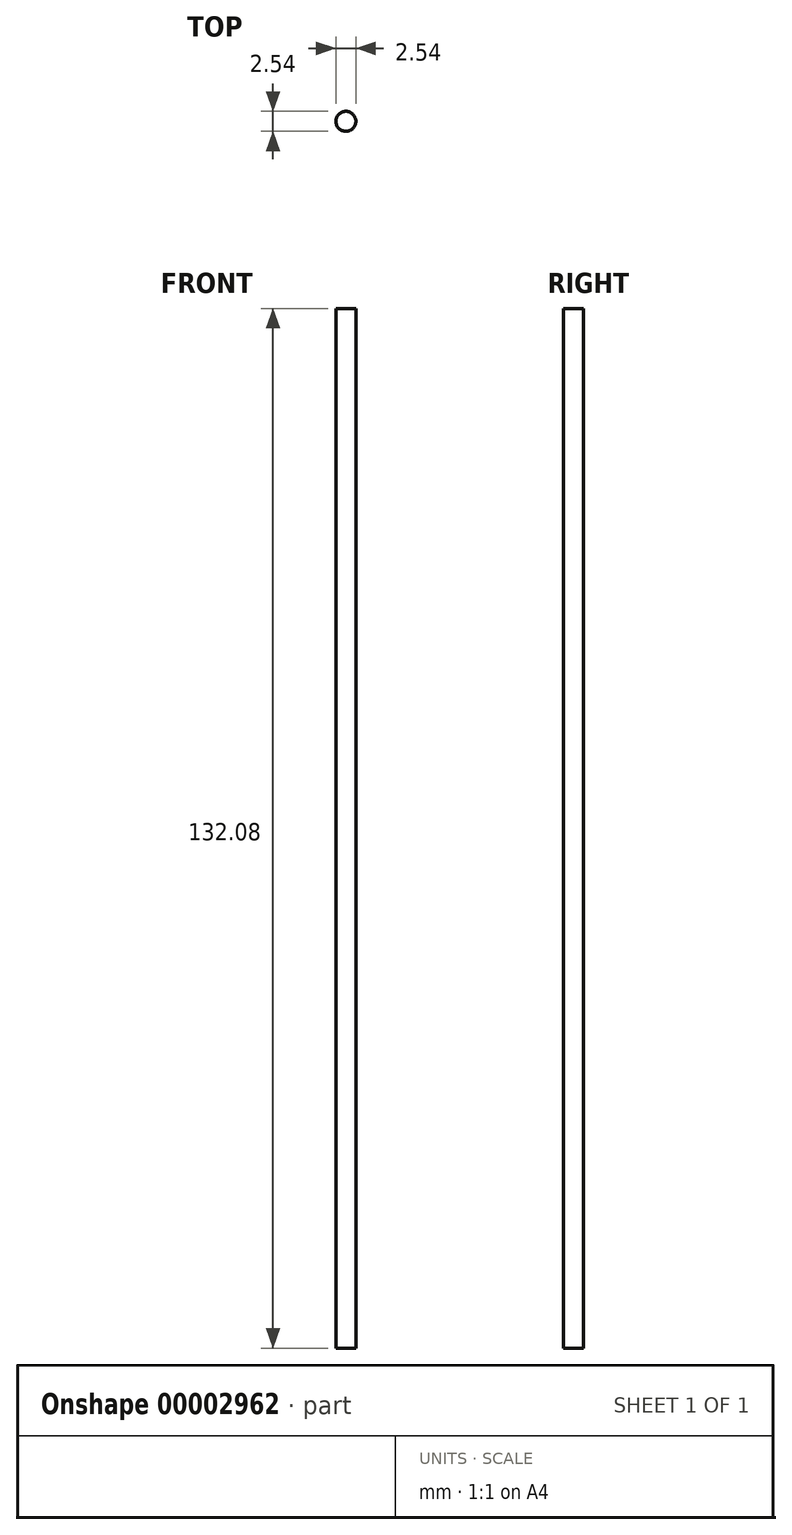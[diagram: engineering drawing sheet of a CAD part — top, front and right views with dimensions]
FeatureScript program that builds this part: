
annotation { "Feature Type Name" : "Feature", "Feature Type Description" : "" }
export const myFeature = defineFeature(function(context is Context, id is Id, definition is map)
    precondition{}
    {
        {
            var Q0;
            Q0=qCreatedBy(makeId("Top.planeOp"),FACE);
            var sketch = newSketch(context, id + "F0", { "sketchPlane" : qUnion([Q0])});
            skCircle(sketch, "E0", {"center": v(0, 0) * mm, "radius": 1.27 * mm});
            skSolve(sketch);
        }
        {
            var Q0;
            Q0=makeQuery(id+"F0.imprint","IMPRINT",FACE,{"disambiguationData":[TD([[makeQuery(id+"F0.imprint","IMPRINT",EDGE,{"derivedFrom":sQuery(id+"F0.wireOp",EDGE,"E0")}),1.0]])]});
            extrude(context, id + "F1", {"entities" : qUnion([Q0]), "depth" : 132.08 * mm});
        }
    });
